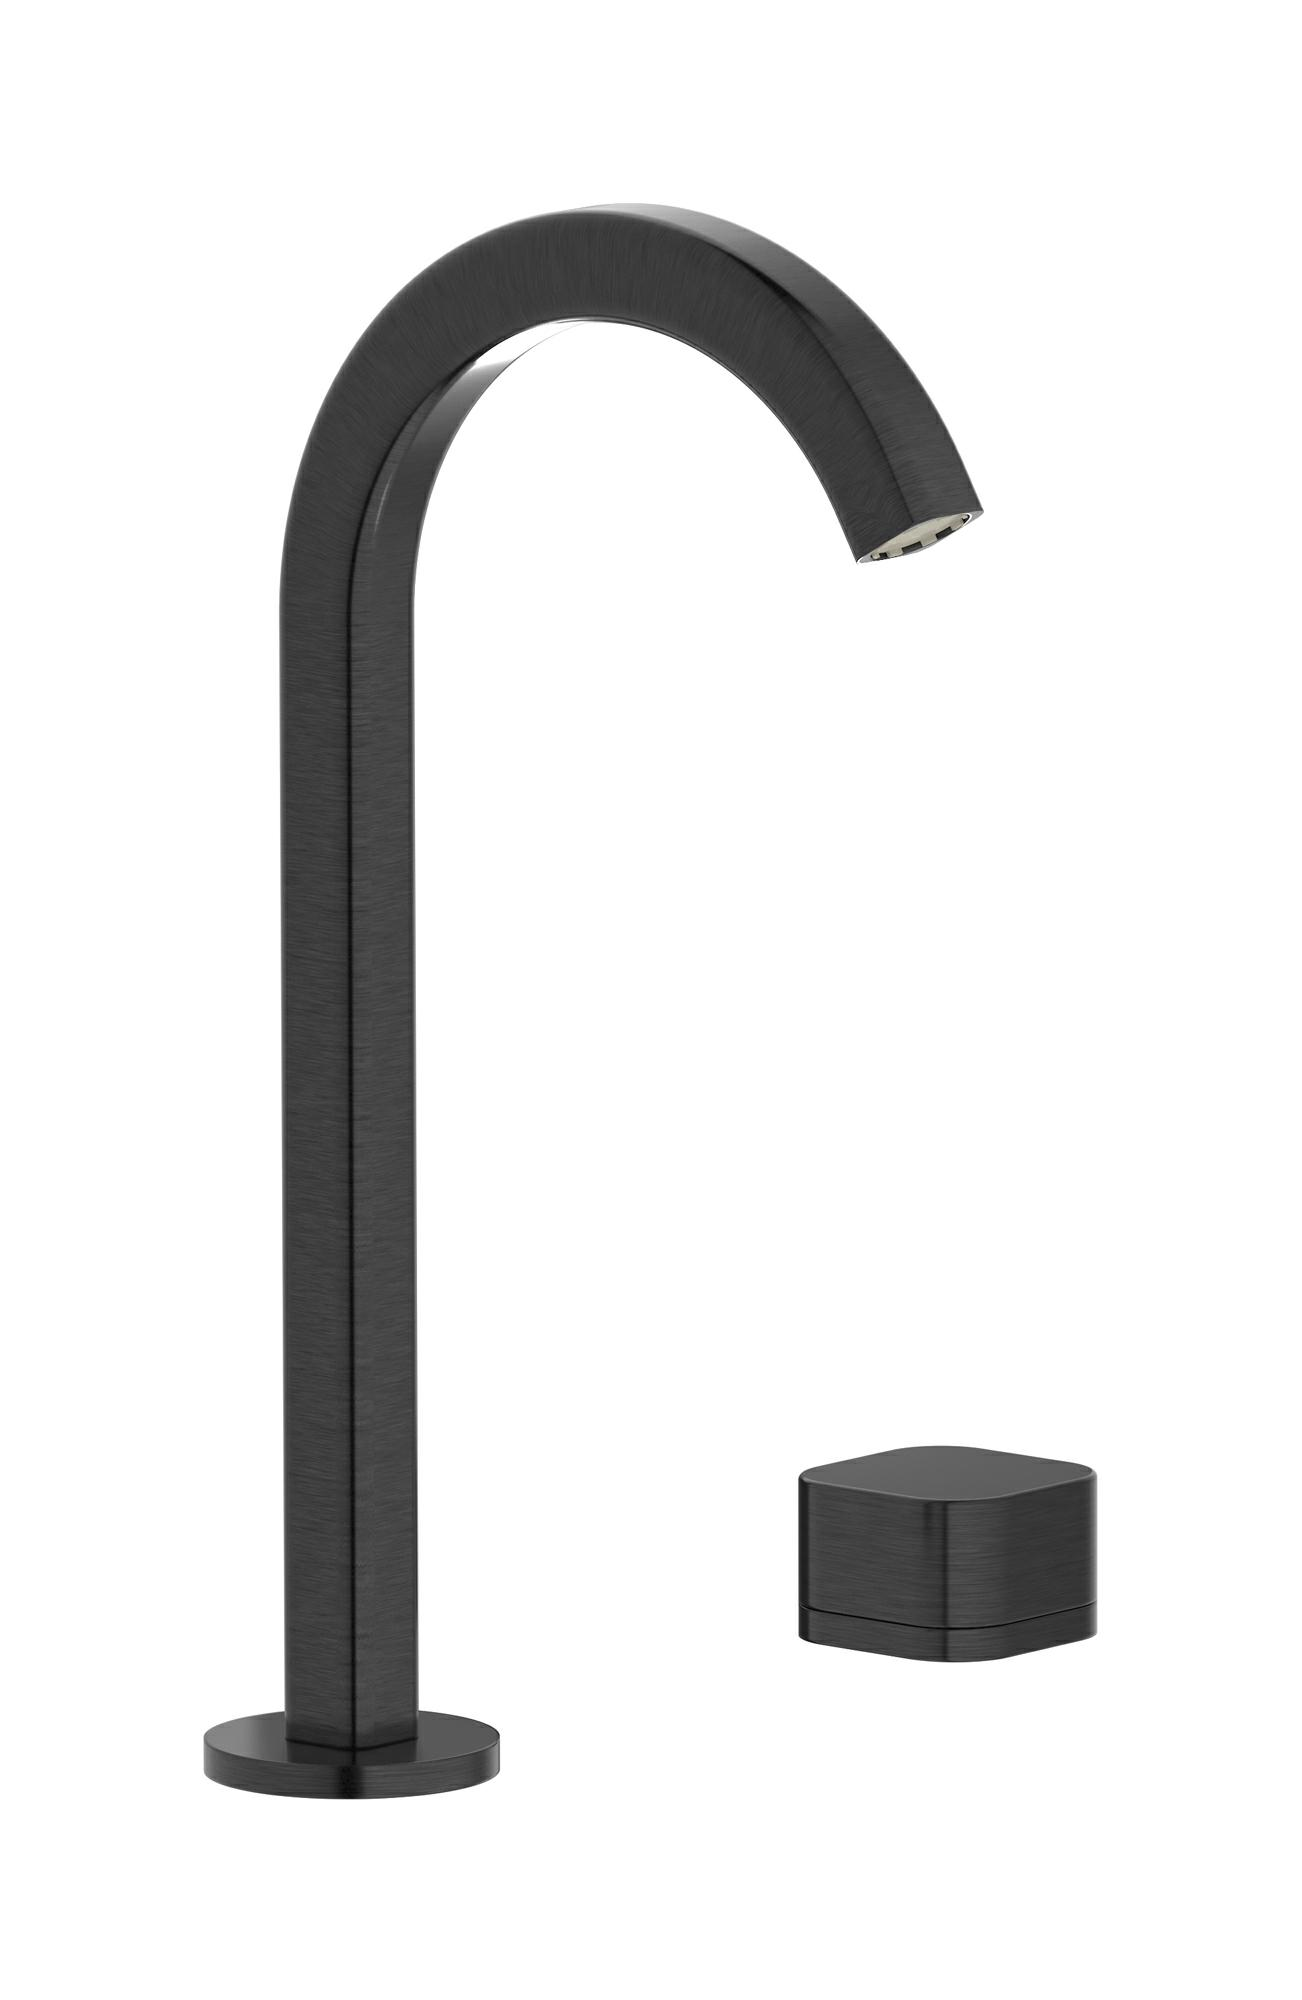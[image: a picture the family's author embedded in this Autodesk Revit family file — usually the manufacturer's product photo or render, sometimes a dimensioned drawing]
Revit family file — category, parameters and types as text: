
# Revit family: EO394_1
name_source: partatom
category: Apparecchi idraulici
units: mm (PartAtom-declared; Revit-internal decimal feet)

## family parameters
Basato su piano di lavoro = No
Condiviso = No
Mantieni orientamento annotazione = No
Numero OmniClass = 23.45.55.17
Punto di calcolo locali = No
Quota connettore circolare = Usa diametro
Sempre verticale = Sì
Taglio con vuoti quando caricato = No
Tipo di parte = Normale
Titolo OmniClass = Mixing Faucets

## types (12) — shared parameters
Cold water inlet = 10 mm  [stored 0.0328084 ft]
Commenti sul tipo = Washbasin
Connessione CW = No
Connessione HW = No
Connessione di scarico = No
Connessione di ventilazione = No
Descrizione = Washbasin two hole mixer
Hot water inlet = 10 mm  [stored 0.0328084 ft]
Produttore = IB Rubinetterie S.p.A.
URL = https://www.weareib.it
zero-valued in all types: Prospetto di default

## per-type parameters (varying)
| type | Finishes surface | Immagine tipo | Modello |
| Chrome | IB_Chrome | EO394CC_1.jpg | EO394CC_1 |
| Brushed nickel | IB_Brushed nickel | EO394SS_1.jpg | EO394SS_1 |
| Matt black | IB_matt black | EO394NP_1.jpg | EO394NP_1 |
| Natural brass | IB_Brass | EO394ON_1.jpg | EO394ON_1 |
| Black chrome | IB_Black chrome | EO394CF_1.jpg | EO394CF_1 |
| Brushed black chrome | IB_Brushed black chrome | EO394CS_1.jpg | EO394CS_1 |
| Pale gold | IB_Pale gold | EO394II_1.jpg | EO394II_1 |
| Brushed pale gold | IB_brushed pale gold | EO394IS_1.jpg | EO394IS_1 |
| Rose gold | IB_Rose gold | EO394RS_1.jpg | EO394RS_1 |
| Brushed rose gold | IB_Brushed rose gold | EO394SR_1.jpg | EO394SR_1 |
| Gold | IB_gold | EO394OO_1.jpg | EO394OO_1 |
| Brushed gold | IB_brushed gold | EO394OS_1.jpg | EO394OS_1 |

note: [stored X ft] marks values corroborated as IEEE doubles in the binary element streams (Revit-internal decimal feet)
